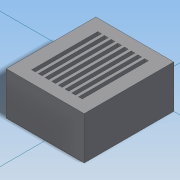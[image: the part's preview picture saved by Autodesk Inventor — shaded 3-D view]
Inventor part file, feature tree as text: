
AUTODESK INVENTOR PART (.ipt)
format: ipt  version: 2014 SP2 (Build 180246200, 246)  size: 227,328 bytes
history: native  units: in
note: dims shown in document units (in); Inventor stores cm internally (conversion verified against a paired STEP export)
features: extrude x5, fillet x5, sketch x5, projected_geometry x3, pattern_linear x1, chamfer x1
ambient origin geometry x8: Origin, YZ Plane, XZ Plane, XY Plane, X Axis, Y Axis, Z Axis, Center Point
bodies: Solid1 (feature_tree)
feature tree (20):
  extrude  "Extrusion1"  Depth=0.8661in
  extrude  "Heatsink Cut"  Depth=1.0236in
  extrude  "Heatsink Fin"  Depth=0.1969in TaperAngle=0.0deg
  pattern_linear  "Rectangular Pattern1"  Spacing1=0.0763in  [1 undecoded]
  fillet  "Fillet4"  Radius=0.1969in
  extrude  "Wires and Caps Bundle"  Depth=0.1353in
  extrude  "Output Wires Bundle"  Depth=0.1772in
  chamfer  "Chamfer1"  Distance=0.7087in
  fillet  "Fillet1"  Radius=1.0236in
  fillet  "Fillet2"  Radius=0.1772in
  fillet  "Fillet3"  Radius=0.7244in
  fillet  "Fillet5"  Radius=0.5in
  sketch  "Sketch1"  dims[d0=1.5748in d1=0.8661in]
  sketch  "Sketch2"  dims[d2=1.811in d3=0.0in d4=1.0236in]
  projected_geometry  "Projected Loop1"
  sketch  "Sketch3"  dims[d5=1.3386in d6=0.1969in d7=0.0in]
  projected_geometry  "Projected Loop2"
  sketch  "Sketch4"  dims[d8=0.0591in]
  projected_geometry  "Projected Loop3"
  sketch  "Sketch5"  dims[d9=1.0236in d10=0.0763in d11=0.1969in d12=0.0in d13=2.7559in d15=0.1353in d16=0.1772in d17=0.7087in d18=1.0236in d19=0.0in d20=0.1772in d21=0.1772in d22=45.0deg d23=0.7244in d24=0.5in d25=0.0787in d26=0.1in d27=0.025in d28=1.1811in d29=0.3937in d30=0.2677in d32=0.7205in d33=0.0in d34=0.25in]
note: 1 required parameter value undecoded (feature->parameter linkage not recoverable at this tier; creation-order binding heuristic only, values carry confidence <= 0.55)
